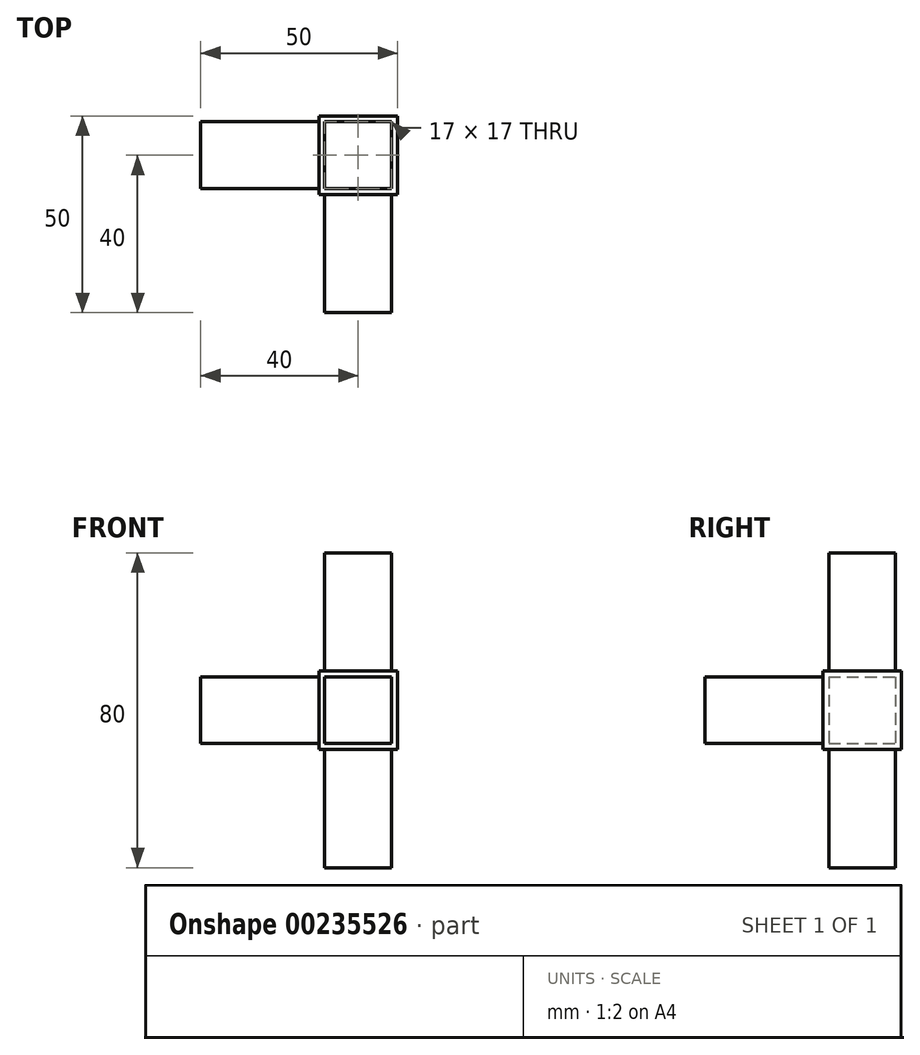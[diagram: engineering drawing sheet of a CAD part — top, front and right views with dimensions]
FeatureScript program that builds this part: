
annotation { "Feature Type Name" : "Feature", "Feature Type Description" : "" }
export const myFeature = defineFeature(function(context is Context, id is Id, definition is map)
    precondition{}
    {
        {
            var Q0;
            Q0=qCreatedBy(makeId("Top.planeOp"),FACE);
            var sketch = newSketch(context, id + "F0", { "sketchPlane" : qUnion([Q0])});
            skLineSegment(sketch, "E0.bottom", {"start": v(10, -10) * mm, "end": v(-10, -10) * mm});
            skLineSegment(sketch, "E0.top", {"start": v(10, 10) * mm, "end": v(-10, 10) * mm});
            skLineSegment(sketch, "E0.left", {"start": v(10, -10) * mm, "end": v(10, 10) * mm});
            skLineSegment(sketch, "E0.right", {"start": v(-10, -10) * mm, "end": v(-10, 10) * mm});
            skPoint(sketch, "E0.middle", {"position": v(0, 0) * mm});
            skLineSegment(sketch, "E1", {"start": v(0, -10) * mm, "end": v(8.5, -10) * mm});
            skLineSegment(sketch, "E2.bottom", {"start": v(8.5, -10) * mm, "end": v(-8.5, -10) * mm});
            skLineSegment(sketch, "E2.top", {"start": v(8.5, -40) * mm, "end": v(-8.5, -40) * mm});
            skLineSegment(sketch, "E2.left", {"start": v(8.5, -10) * mm, "end": v(8.5, -40) * mm});
            skLineSegment(sketch, "E2.right", {"start": v(-8.5, -10) * mm, "end": v(-8.5, -40) * mm});
            skLineSegment(sketch, "E3", {"start": v(-10, 0) * mm, "end": v(-10, -8.5) * mm});
            skLineSegment(sketch, "E4.bottom", {"start": v(-10, -8.5) * mm, "end": v(-40, -8.5) * mm});
            skLineSegment(sketch, "E4.top", {"start": v(-10, 8.5) * mm, "end": v(-40, 8.5) * mm});
            skLineSegment(sketch, "E4.left", {"start": v(-10, -8.5) * mm, "end": v(-10, 8.5) * mm});
            skLineSegment(sketch, "E4.right", {"start": v(-40, -8.5) * mm, "end": v(-40, 8.5) * mm});
            skSolve(sketch);
        }
        {
            var Q0;
            {var subQ1=sQuery(id+"F0.wireOp",EDGE,"E0.top");Q0=makeQuery(id+"F0.imprint","IMPRINT",FACE,{"disambiguationData":[TD([[makeQuery(id+"F0.imprint","IMPRINT",EDGE,{"derivedFrom":subQ1}),1.0]])]});}
            extrude(context, id + "F1", {"entities" : qUnion([Q0]), "depth" : 20 * mm});
        }
        {
            var Q0;
            {var subQ4=sQuery(id+"F0.wireOp",EDGE,"E4.bottom");Q0=makeQuery(id+"F0.imprint","IMPRINT",FACE,{"disambiguationData":[TD([[makeQuery(id+"F0.imprint","IMPRINT",EDGE,{"derivedFrom":subQ4}),-1.0]])]});}
            var Q1;
            Q1=makeQuery(id+"F0.imprint","IMPRINT",FACE,{"disambiguationData":[TD([[makeQuery(id+"F0.imprint","IMPRINT",EDGE,{"derivedFrom":sQuery(id+"F0.wireOp",EDGE,"E2.top")}),-1.0]])]});
            extrude(context, id + "F2", {"entities" : qUnion([Q0, Q1]), "operationType" : NewBodyOperationType.ADD, "depth" : 18.5 * mm, "hasSecondDirection" : true, "secondDirectionOppositeDirection" : false, "secondDirectionDepth" : 1.5 * mm});
        }
        {
            var Q0;
            Q0=makeQuery(id+"F1.opExtrude","CAP_FACE",FACE,{"disambiguationData":[OSD([sQuery(id+"F0.wireOp",EDGE,"E0.bottom"),sQuery(id+"F0.wireOp",EDGE,"E0.top"),sQuery(id+"F0.wireOp",EDGE,"E0.left"),sQuery(id+"F0.wireOp",EDGE,"E0.right"),sQuery(id+"F0.wireOp",EDGE,"E2.bottom"),sQuery(id+"F0.wireOp",EDGE,"E4.left")])],"isStart":false});
            var sketch = newSketch(context, id + "F3", { "sketchPlane" : qUnion([Q0])});
            skLineSegment(sketch, "E5.bottom", {"start": v(8.5, -8.5) * mm, "end": v(-8.5, -8.5) * mm});
            skLineSegment(sketch, "E5.top", {"start": v(8.5, 8.5) * mm, "end": v(-8.5, 8.5) * mm});
            skLineSegment(sketch, "E5.left", {"start": v(8.5, -8.5) * mm, "end": v(8.5, 8.5) * mm});
            skLineSegment(sketch, "E5.right", {"start": v(-8.5, -8.5) * mm, "end": v(-8.5, 8.5) * mm});
            skPoint(sketch, "E5.middle", {"position": v(0, 0) * mm});
            skSolve(sketch);
        }
        {
            var Q0;
            Q0=qSketchRegion(id+"F3",true);
            extrude(context, id + "F4", {"entities" : qUnion([Q0]), "operationType" : NewBodyOperationType.ADD, "depth" : 30 * mm});
        }
        {
            var Q0;
            Q0=makeQuery(id+"F1.opExtrude","CAP_FACE",FACE,{"disambiguationData":[OSD([sQuery(id+"F0.wireOp",EDGE,"E0.bottom"),sQuery(id+"F0.wireOp",EDGE,"E0.top"),sQuery(id+"F0.wireOp",EDGE,"E0.left"),sQuery(id+"F0.wireOp",EDGE,"E0.right"),sQuery(id+"F0.wireOp",EDGE,"E2.bottom"),sQuery(id+"F0.wireOp",EDGE,"E4.left")])],"isStart":true});
            var sketch = newSketch(context, id + "F5", { "sketchPlane" : qUnion([Q0])});
            skLineSegment(sketch, "E6.bottom", {"start": v(8.5, -8.5) * mm, "end": v(-8.5, -8.5) * mm});
            skLineSegment(sketch, "E6.top", {"start": v(8.5, 8.5) * mm, "end": v(-8.5, 8.5) * mm});
            skLineSegment(sketch, "E6.left", {"start": v(8.5, -8.5) * mm, "end": v(8.5, 8.5) * mm});
            skLineSegment(sketch, "E6.right", {"start": v(-8.5, -8.5) * mm, "end": v(-8.5, 8.5) * mm});
            skPoint(sketch, "E6.middle", {"position": v(0, 0) * mm});
            skSolve(sketch);
        }
        {
            var Q0;
            Q0 = qSketchRegion(id + "F5", true);
            extrude(context, id + "F6", {"entities" : qUnion([Q0]), "operationType" : NewBodyOperationType.ADD, "depth" : 30 * mm});
        }
    });
